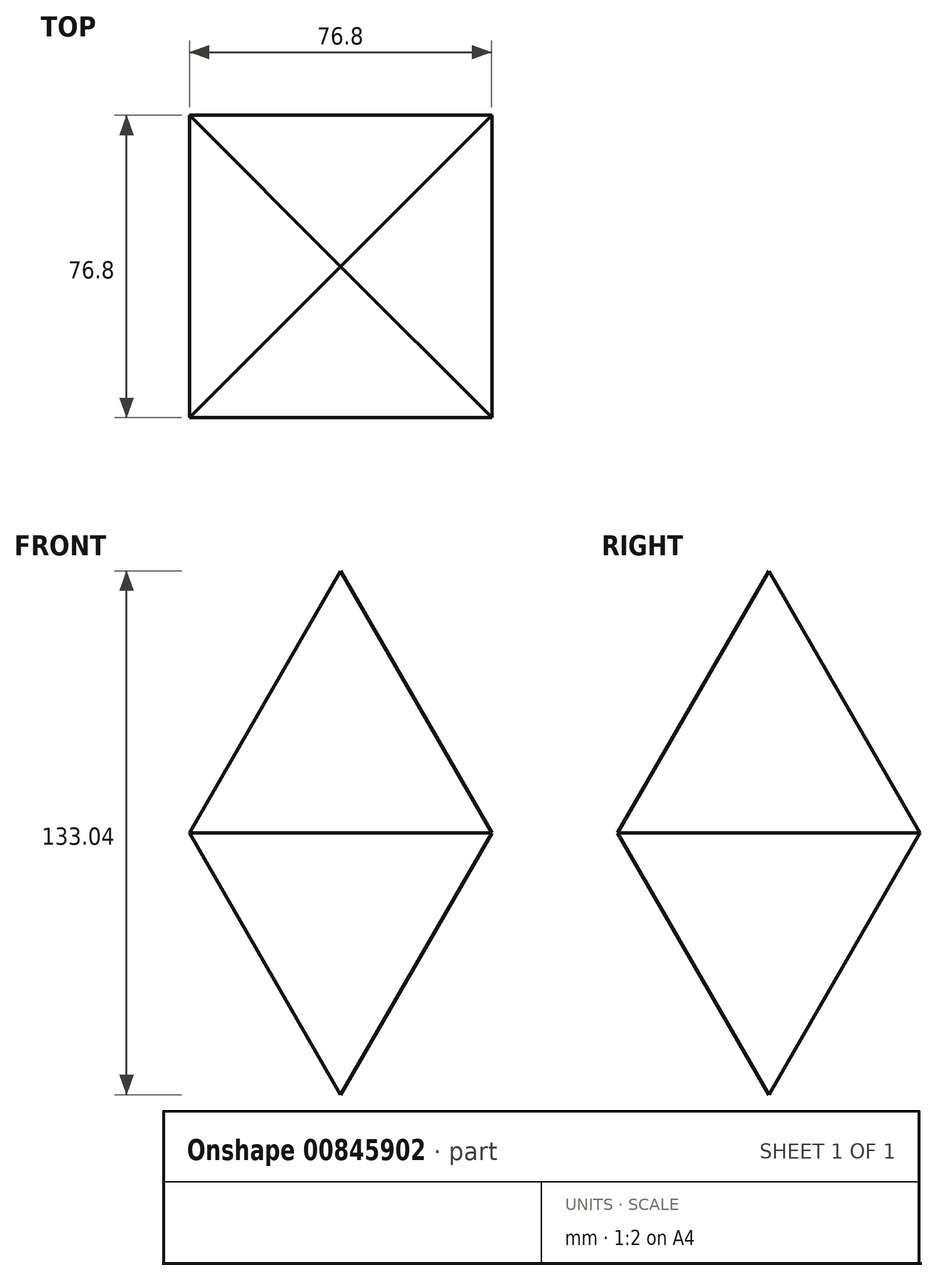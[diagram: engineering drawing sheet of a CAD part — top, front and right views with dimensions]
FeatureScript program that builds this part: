
annotation { "Feature Type Name" : "Feature", "Feature Type Description" : "" }
export const myFeature = defineFeature(function(context is Context, id is Id, definition is map)
    precondition{}
    {
        {
            var Q0;
            Q0=qCreatedBy(makeId("Top.planeOp"),FACE);
            var sketch = newSketch(context, id + "F0", { "sketchPlane" : qUnion([Q0])});
            skLineSegment(sketch, "E0.bottom", {"start": v(38.4, 38.4) * mm, "end": v(-38.4, 38.4) * mm});
            skLineSegment(sketch, "E0.top", {"start": v(38.4, -38.4) * mm, "end": v(-38.4, -38.4) * mm});
            skLineSegment(sketch, "E0.left", {"start": v(38.4, 38.4) * mm, "end": v(38.4, -38.4) * mm});
            skLineSegment(sketch, "E0.right", {"start": v(-38.4, 38.4) * mm, "end": v(-38.4, -38.4) * mm});
            skPoint(sketch, "E0.middle", {"position": v(0, 0) * mm});
            skSolve(sketch);
        }
        {
            var Q0;
            Q0=makeQuery(id+"F0.imprint","IMPRINT",FACE,{"disambiguationData":[TD([[makeQuery(id+"F0.imprint","IMPRINT",EDGE,{"derivedFrom":sQuery(id+"F0.wireOp",EDGE,"E0.bottom")}),1.0]])]});
            extrude(context, id + "F1", {"entities" : qUnion([Q0]), "depth" : 80 * mm, "offsetDistance" : 25.4 * mm, "hasDraft" : true, "draftAngle" : 30 * degree, "draftPullDirection" : true, "hasSecondDirection" : true, "secondDirectionOppositeDirection" : true, "secondDirectionDepth" : 90.93 * mm, "hasSecondDirectionDraft" : true, "secondDirectionDraftAngle" : 30 * degree, "secondDirectionDraftPullDirection" : true});
        }
    });
